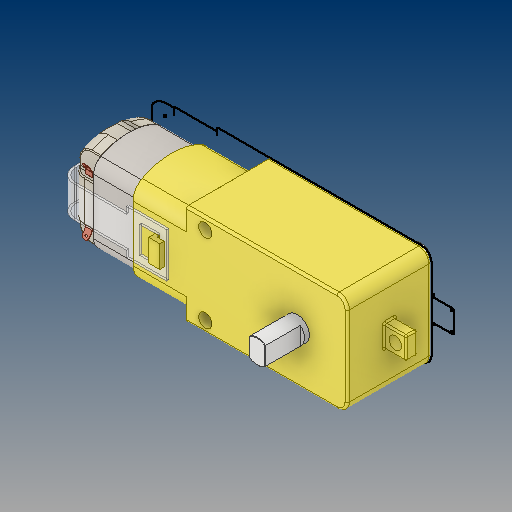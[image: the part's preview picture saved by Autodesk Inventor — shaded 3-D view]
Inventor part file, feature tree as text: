
AUTODESK INVENTOR PART (.ipt)
format: ipt  version: 2017 (Build 210142000, 142)  size: 570,368 bytes
history: mixed  units: in
note: dims shown in document units (in); Inventor stores cm internally (conversion verified against a paired STEP export)
features: fillet x4, other x3, sketch x1, chamfer x1, mirror x1, imported_body x1
ambient origin geometry x8: Origin, YZ Plane, XZ Plane, XY Plane, X Axis, Y Axis, Z Axis, Center Point
bodies: Solid1 (imported_parasolid), Solid2 (imported_parasolid), Solid3 (imported_parasolid), Solid4 (imported_parasolid), Solid5 (imported_parasolid), Solid6 (imported_parasolid), Solid7 (imported_parasolid), Solid8 (imported_parasolid), Solid9 (imported_parasolid)
feature tree (11):
  sketch  "Sketch4"
  other  "Cortar-Extruir7"
  fillet  "Redondeo8"  [1 undecoded]
  fillet  "Redondeo2"  [1 undecoded]
  fillet  "Redondeo10"  [1 undecoded]
  fillet  "Redondeo14"  [1 undecoded]
  chamfer  "Chaflán1"  [1 undecoded]
  other  "Cortar-Extruir9[1]"
  other  "Cortar-Extruir9[2]"
  mirror  "Simetría2"
  imported_body  NMx_Import_Brep_tag  [imported B-rep: ~80 faces, bbox_mm=[64.7, 18.598921, 36.8]]
note: 5 required parameter values undecoded (feature->parameter linkage not recoverable at this tier; creation-order binding heuristic only, values carry confidence <= 0.55)
